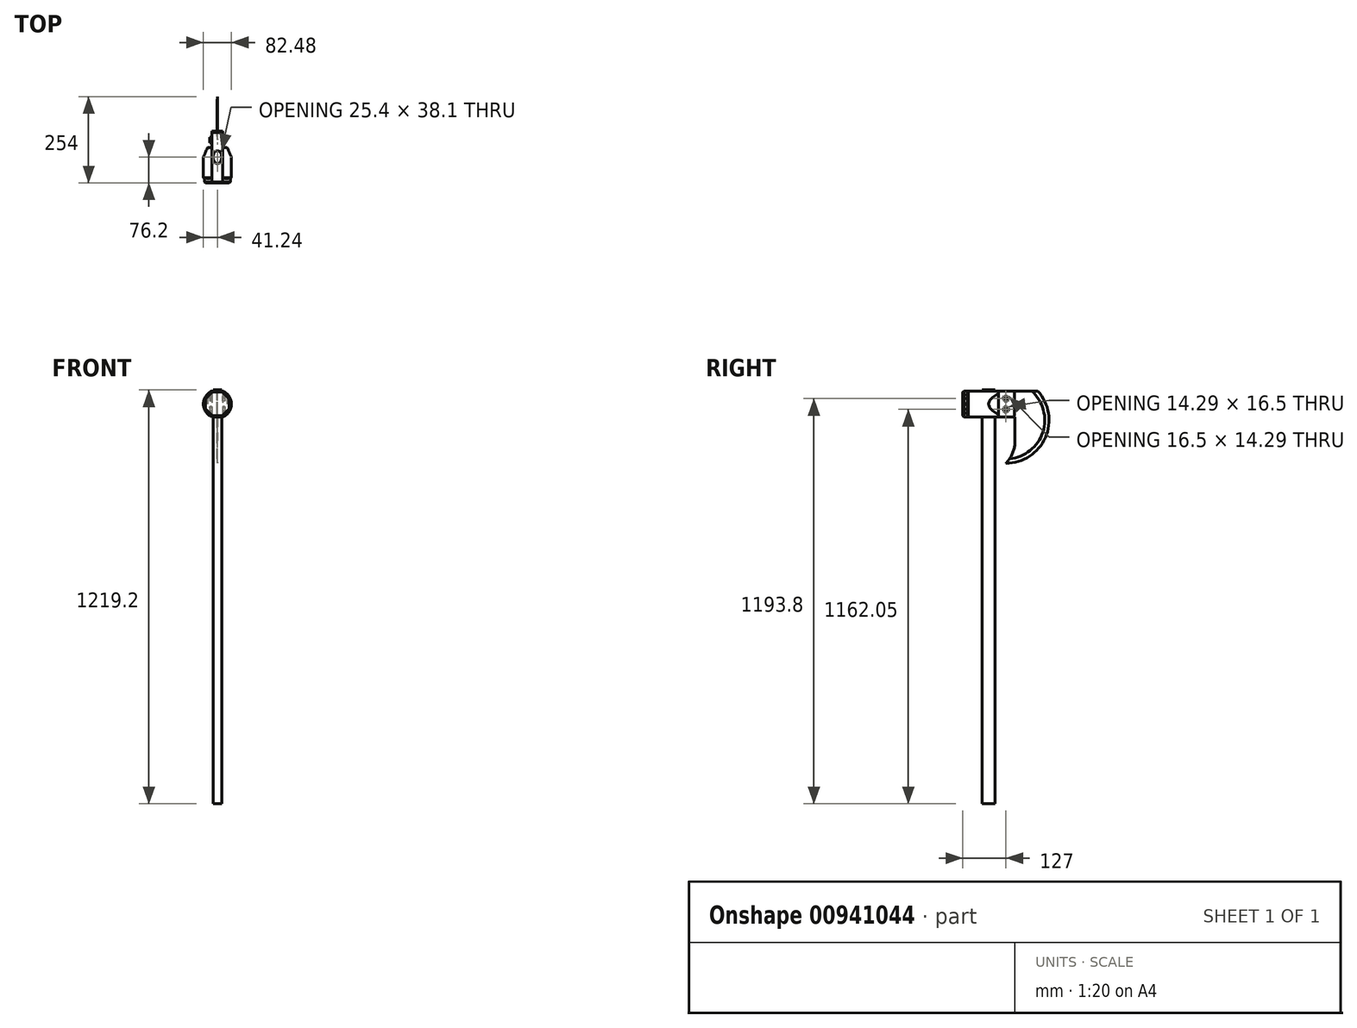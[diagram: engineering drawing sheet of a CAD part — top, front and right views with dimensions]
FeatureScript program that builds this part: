
annotation { "Feature Type Name" : "Feature", "Feature Type Description" : "" }
export const myFeature = defineFeature(function(context is Context, id is Id, definition is map)
    precondition{}
    {
        {
            var Q0;
            Q0=qCreatedBy(makeId("Top.planeOp"),FACE);
            var sketch = newSketch(context, id + "F0", { "sketchPlane" : qUnion([Q0])});
            skEllipse(sketch, "E0", {"center": v(0, 0) * mm, "majorRadius": 12.7 * mm, "minorRadius": 19.05 * mm, "majorAxis": v(1, 0)});
            skSolve(sketch);
        }
        {
            var Q0;
            Q0 = qSketchRegion(id + "F0", true);
            extrude(context, id + "F1", {"entities" : qUnion([Q0]), "depth" : 1219.2 * mm, "offsetDistance" : 25.4 * mm});
        }
        {
            var Q0;
            Q0=qCreatedBy(makeId("Front.planeOp"),FACE);
            var sketch = newSketch(context, id + "F2", { "sketchPlane" : qUnion([Q0])});
            skCircle(sketch, "E1.cCircle", {"center": v(0, 1177.93) * mm, "radius": 41.24 * mm});
            skLineSegment(sketch, "E1.0", {"start": v(15.78, 1139.83) * mm, "end": v(-15.78, 1139.83) * mm});
            skLineSegment(sketch, "E1.1", {"start": v(-15.78, 1139.83) * mm, "end": v(-38.1, 1162.14) * mm});
            skLineSegment(sketch, "E1.2", {"start": v(-38.1, 1162.14) * mm, "end": v(-38.1, 1193.7) * mm});
            skLineSegment(sketch, "E1.3", {"start": v(-38.1, 1193.7) * mm, "end": v(-15.78, 1216.03) * mm});
            skLineSegment(sketch, "E1.4", {"start": v(-15.78, 1216.03) * mm, "end": v(15.78, 1216.03) * mm});
            skLineSegment(sketch, "E1.5", {"start": v(15.78, 1216.03) * mm, "end": v(38.1, 1193.7) * mm});
            skLineSegment(sketch, "E1.6", {"start": v(38.1, 1193.7) * mm, "end": v(38.1, 1162.14) * mm});
            skLineSegment(sketch, "E1.7", {"start": v(38.1, 1162.14) * mm, "end": v(15.78, 1139.83) * mm});
            skSolve(sketch);
        }
        {
            var Q0;
            Q0=makeQuery(id+"F2.imprint","IMPRINT",FACE,{"disambiguationData":[TD([[makeQuery(id+"F2.imprint","IMPRINT",EDGE,{"derivedFrom":sQuery(id+"F2.wireOp",EDGE,"E1.0")}),-1.0]])]});
            extrude(context, id + "F3", {"entities" : qUnion([Q0]), "operationType" : NewBodyOperationType.ADD, "depth" : 76.2 * mm, "offsetDistance" : 25.4 * mm, "hasSecondDirection" : true, "secondDirectionOppositeDirection" : true, "secondDirectionDepth" : 76.2 * mm});
        }
        {
            var Q0;
            {var subQ0=sQuery(id+"F2.wireOp",EDGE,"E1.5");Q0=makeQuery(id+"F2.imprint","IMPRINT",FACE,{"disambiguationData":[TD([[makeQuery(id+"F2.imprint","IMPRINT",EDGE,{"derivedFrom":subQ0}),1.0]])]});}
            var Q1;
            {var subQ0=sQuery(id+"F2.wireOp",EDGE,"E1.6");Q1=makeQuery(id+"F2.imprint","IMPRINT",FACE,{"disambiguationData":[TD([[makeQuery(id+"F2.imprint","IMPRINT",EDGE,{"derivedFrom":subQ0}),1.0]])]});}
            var Q2;
            {var subQ0=sQuery(id+"F2.wireOp",EDGE,"E1.7");Q2=makeQuery(id+"F2.imprint","IMPRINT",FACE,{"disambiguationData":[TD([[makeQuery(id+"F2.imprint","IMPRINT",EDGE,{"derivedFrom":subQ0}),1.0]])]});}
            var Q3;
            {var subQ0=sQuery(id+"F2.wireOp",EDGE,"E1.1");Q3=makeQuery(id+"F2.imprint","IMPRINT",FACE,{"disambiguationData":[TD([[makeQuery(id+"F2.imprint","IMPRINT",EDGE,{"derivedFrom":subQ0}),1.0]])]});}
            var Q4;
            {var subQ0=sQuery(id+"F2.wireOp",EDGE,"E1.2");Q4=makeQuery(id+"F2.imprint","IMPRINT",FACE,{"disambiguationData":[TD([[makeQuery(id+"F2.imprint","IMPRINT",EDGE,{"derivedFrom":subQ0}),1.0]])]});}
            var Q5;
            {var subQ0=sQuery(id+"F2.wireOp",EDGE,"E1.3");Q5=makeQuery(id+"F2.imprint","IMPRINT",FACE,{"disambiguationData":[TD([[makeQuery(id+"F2.imprint","IMPRINT",EDGE,{"derivedFrom":subQ0}),1.0]])]});}
            extrude(context, id + "F4", {"entities" : qUnion([Q0, Q1, Q2, Q3, Q4, Q5]), "operationType" : NewBodyOperationType.ADD, "depth" : 63.5 * mm, "offsetDistance" : 25.4 * mm, "hasSecondDirection" : true, "secondDirectionOppositeDirection" : true, "secondDirectionDepth" : 63.5 * mm});
        }
        {
            var Q0;
            Q0=makeQuery(id+"F3.opExtrude","CAP_FACE",FACE,{"disambiguationData":[OSD([sQuery(id+"F2.wireOp",EDGE,"E1.0"),sQuery(id+"F2.wireOp",EDGE,"E1.1"),sQuery(id+"F2.wireOp",EDGE,"E1.2"),sQuery(id+"F2.wireOp",EDGE,"E1.3"),sQuery(id+"F2.wireOp",EDGE,"E1.4"),sQuery(id+"F2.wireOp",EDGE,"E1.5"),sQuery(id+"F2.wireOp",EDGE,"E1.6"),sQuery(id+"F2.wireOp",EDGE,"E1.7")])],"isStart":false});
            var Q1;
            Q1=makeQuery(id+"F3.opExtrude","CAP_FACE",FACE,{"disambiguationData":[OSD([sQuery(id+"F2.wireOp",EDGE,"E1.0"),sQuery(id+"F2.wireOp",EDGE,"E1.1"),sQuery(id+"F2.wireOp",EDGE,"E1.2"),sQuery(id+"F2.wireOp",EDGE,"E1.3"),sQuery(id+"F2.wireOp",EDGE,"E1.4"),sQuery(id+"F2.wireOp",EDGE,"E1.5"),sQuery(id+"F2.wireOp",EDGE,"E1.6"),sQuery(id+"F2.wireOp",EDGE,"E1.7")])],"isStart":true});
            chamfer(context, id + "F5", {"entities" : qUnion([Q0, Q1]), "width" : 3.17 * mm, "tangentPropagation" : true});
        }
        {
            var Q0;
            {var subQ0=sQuery(id+"F2.wireOp",EDGE,"E1.3");var subQ1=sQuery(id+"F2.wireOp",EDGE,"E1.cCircle");Q0=makeQuery(id+"F4.opExtrude","CAP_EDGE",EDGE,{"disambiguationData":[OSD([subQ1]),TDD([makeQuery(id+"F2.imprint","IMPRINT",EDGE,{"disambiguationData":[TD([[makeQuery(id+"F2.imprint","INTERSECT",VERTEX,{"derivedFrom":[subQ1,sQuery(id+"F2.wireOp",EDGE,"E1.2"),subQ0]}),1.0]])],"derivedFrom":subQ1})])],"isStart":true});}
            var Q1;
            {var subQ0=sQuery(id+"F2.wireOp",EDGE,"E1.2");var subQ1=sQuery(id+"F2.wireOp",EDGE,"E1.cCircle");Q1=makeQuery(id+"F4.opExtrude","CAP_EDGE",EDGE,{"disambiguationData":[OSD([subQ1]),TDD([makeQuery(id+"F2.imprint","IMPRINT",EDGE,{"disambiguationData":[TD([[makeQuery(id+"F2.imprint","INTERSECT",VERTEX,{"derivedFrom":[subQ1,sQuery(id+"F2.wireOp",EDGE,"E1.1"),subQ0]}),1.0]])],"derivedFrom":subQ1})])],"isStart":true});}
            var Q2;
            {var subQ0=sQuery(id+"F2.wireOp",EDGE,"E1.1");var subQ1=sQuery(id+"F2.wireOp",EDGE,"E1.cCircle");Q2=makeQuery(id+"F4.opExtrude","CAP_EDGE",EDGE,{"disambiguationData":[OSD([subQ1]),TDD([makeQuery(id+"F2.imprint","IMPRINT",EDGE,{"disambiguationData":[TD([[makeQuery(id+"F2.imprint","INTERSECT",VERTEX,{"derivedFrom":[subQ1,sQuery(id+"F2.wireOp",EDGE,"E1.0"),subQ0]}),1.0]])],"derivedFrom":subQ1})])],"isStart":true});}
            var Q3;
            {var subQ0=sQuery(id+"F2.wireOp",EDGE,"E1.5");var subQ1=sQuery(id+"F2.wireOp",EDGE,"E1.cCircle");Q3=makeQuery(id+"F4.opExtrude","CAP_EDGE",EDGE,{"disambiguationData":[OSD([subQ1]),TDD([makeQuery(id+"F2.imprint","IMPRINT",EDGE,{"disambiguationData":[TD([[makeQuery(id+"F2.imprint","INTERSECT",VERTEX,{"derivedFrom":[subQ1,sQuery(id+"F2.wireOp",EDGE,"E1.4"),subQ0]}),1.0]])],"derivedFrom":subQ1})])],"isStart":true});}
            var Q4;
            {var subQ0=sQuery(id+"F2.wireOp",EDGE,"E1.6");var subQ1=sQuery(id+"F2.wireOp",EDGE,"E1.cCircle");Q4=makeQuery(id+"F4.opExtrude","CAP_EDGE",EDGE,{"disambiguationData":[OSD([subQ1]),TDD([makeQuery(id+"F2.imprint","IMPRINT",EDGE,{"disambiguationData":[TD([[makeQuery(id+"F2.imprint","INTERSECT",VERTEX,{"derivedFrom":[subQ1,sQuery(id+"F2.wireOp",EDGE,"E1.5"),subQ0]}),1.0]])],"derivedFrom":subQ1})])],"isStart":true});}
            var Q5;
            {var subQ0=sQuery(id+"F2.wireOp",EDGE,"E1.7");var subQ1=sQuery(id+"F2.wireOp",EDGE,"E1.cCircle");Q5=makeQuery(id+"F4.opExtrude","CAP_EDGE",EDGE,{"disambiguationData":[OSD([subQ1]),TDD([makeQuery(id+"F2.imprint","IMPRINT",EDGE,{"disambiguationData":[TD([[makeQuery(id+"F2.imprint","INTERSECT",VERTEX,{"derivedFrom":[subQ1,sQuery(id+"F2.wireOp",EDGE,"E1.0"),subQ0]}),-1.0]])],"derivedFrom":subQ1})])],"isStart":true});}
            var Q6;
            {var subQ0=sQuery(id+"F2.wireOp",EDGE,"E1.5");var subQ1=sQuery(id+"F2.wireOp",EDGE,"E1.cCircle");Q6=makeQuery(id+"F4.opExtrude","CAP_EDGE",EDGE,{"disambiguationData":[OSD([subQ1]),TDD([makeQuery(id+"F2.imprint","IMPRINT",EDGE,{"disambiguationData":[TD([[makeQuery(id+"F2.imprint","INTERSECT",VERTEX,{"derivedFrom":[subQ1,sQuery(id+"F2.wireOp",EDGE,"E1.4"),subQ0]}),1.0]])],"derivedFrom":subQ1})])],"isStart":false});}
            var Q7;
            {var subQ0=sQuery(id+"F2.wireOp",EDGE,"E1.6");var subQ1=sQuery(id+"F2.wireOp",EDGE,"E1.cCircle");Q7=makeQuery(id+"F4.opExtrude","CAP_EDGE",EDGE,{"disambiguationData":[OSD([subQ1]),TDD([makeQuery(id+"F2.imprint","IMPRINT",EDGE,{"disambiguationData":[TD([[makeQuery(id+"F2.imprint","INTERSECT",VERTEX,{"derivedFrom":[subQ1,sQuery(id+"F2.wireOp",EDGE,"E1.5"),subQ0]}),1.0]])],"derivedFrom":subQ1})])],"isStart":false});}
            var Q8;
            {var subQ0=sQuery(id+"F2.wireOp",EDGE,"E1.7");var subQ1=sQuery(id+"F2.wireOp",EDGE,"E1.cCircle");Q8=makeQuery(id+"F4.opExtrude","CAP_EDGE",EDGE,{"disambiguationData":[OSD([subQ1]),TDD([makeQuery(id+"F2.imprint","IMPRINT",EDGE,{"disambiguationData":[TD([[makeQuery(id+"F2.imprint","INTERSECT",VERTEX,{"derivedFrom":[subQ1,sQuery(id+"F2.wireOp",EDGE,"E1.0"),subQ0]}),-1.0]])],"derivedFrom":subQ1})])],"isStart":false});}
            var Q9;
            {var subQ0=sQuery(id+"F2.wireOp",EDGE,"E1.3");var subQ1=sQuery(id+"F2.wireOp",EDGE,"E1.cCircle");Q9=makeQuery(id+"F4.opExtrude","CAP_EDGE",EDGE,{"disambiguationData":[OSD([subQ1]),TDD([makeQuery(id+"F2.imprint","IMPRINT",EDGE,{"disambiguationData":[TD([[makeQuery(id+"F2.imprint","INTERSECT",VERTEX,{"derivedFrom":[subQ1,sQuery(id+"F2.wireOp",EDGE,"E1.2"),subQ0]}),1.0]])],"derivedFrom":subQ1})])],"isStart":false});}
            var Q10;
            {var subQ0=sQuery(id+"F2.wireOp",EDGE,"E1.2");var subQ1=sQuery(id+"F2.wireOp",EDGE,"E1.cCircle");Q10=makeQuery(id+"F4.opExtrude","CAP_EDGE",EDGE,{"disambiguationData":[OSD([subQ1]),TDD([makeQuery(id+"F2.imprint","IMPRINT",EDGE,{"disambiguationData":[TD([[makeQuery(id+"F2.imprint","INTERSECT",VERTEX,{"derivedFrom":[subQ1,sQuery(id+"F2.wireOp",EDGE,"E1.1"),subQ0]}),1.0]])],"derivedFrom":subQ1})])],"isStart":false});}
            var Q11;
            {var subQ0=sQuery(id+"F2.wireOp",EDGE,"E1.1");var subQ1=sQuery(id+"F2.wireOp",EDGE,"E1.cCircle");Q11=makeQuery(id+"F4.opExtrude","CAP_EDGE",EDGE,{"disambiguationData":[OSD([subQ1]),TDD([makeQuery(id+"F2.imprint","IMPRINT",EDGE,{"disambiguationData":[TD([[makeQuery(id+"F2.imprint","INTERSECT",VERTEX,{"derivedFrom":[subQ1,sQuery(id+"F2.wireOp",EDGE,"E1.0"),subQ0]}),1.0]])],"derivedFrom":subQ1})])],"isStart":false});}
            chamfer(context, id + "F6", {"entities" : qUnion([Q0, Q1, Q2, Q3, Q4, Q5, Q6, Q7, Q8, Q9, Q10, Q11]), "width" : 3.12 * mm});
        }
        {
            var Q0;
            Q0=qCreatedBy(makeId("Right.planeOp"),FACE);
            var sketch = newSketch(context, id + "F7", { "sketchPlane" : qUnion([Q0])});
            skCircle(sketch, "E2", {"center": v(50.8, 1130.3) * mm, "radius": 127 * mm});
            skPoint(sketch, "E3.start.orphan", {"position": v(50.8, 1003.3) * mm});
            skLineSegment(sketch, "E4", {"start": v(30.16, 1216.03) * mm, "end": v(30.16, 1139.83) * mm});
            skLineSegment(sketch, "E5", {"start": v(30.16, 1216.03) * mm, "end": v(144.5, 1216.03) * mm});
            skLineSegment(sketch, "E6", {"start": v(30.16, 1139.83) * mm, "end": v(77.79, 1139.83) * mm});
            skLineSegment(sketch, "E7", {"start": v(77.79, 1139.83) * mm, "end": v(77.79, 1069.98) * mm});
            skArc(sketch, "E8", {"start": v(50.8, 1003.3) * mm, "mid": v(70.78, 1034.01) * mm, "end": v(77.79, 1069.98) * mm});
            skSolve(sketch);
        }
        {
            var Q0;
            Q0=makeQuery(id+"F7.imprint","IMPRINT",FACE,{"disambiguationData":[TD([[makeQuery(id+"F7.imprint","IMPRINT",EDGE,{"derivedFrom":sQuery(id+"F7.wireOp",EDGE,"E4")}),1.0]])]});
            extrude(context, id + "F8", {"entities" : qUnion([Q0]), "operationType" : NewBodyOperationType.ADD, "depth" : 0.8 * mm, "offsetDistance" : 25.4 * mm, "hasSecondDirection" : true, "secondDirectionOppositeDirection" : true, "secondDirectionDepth" : 0.8 * mm});
        }
        {
            var Q0;
            Q0=qCreatedBy(makeId("Top.planeOp"),FACE);
            var sketch = newSketch(context, id + "F9", { "sketchPlane" : qUnion([Q0])});
            skLineSegment(sketch, "E9.bottom", {"start": v(28.58, 28.57) * mm, "end": v(15.88, 28.57) * mm});
            skLineSegment(sketch, "E9.top", {"start": v(41.28, 76.2) * mm, "end": v(15.88, 76.2) * mm});
            skLineSegment(sketch, "E9.left", {"start": v(41.27, 28.57) * mm, "end": v(41.28, 76.2) * mm});
            skLineSegment(sketch, "E9.right", {"start": v(-41.28, 28.57) * mm, "end": v(-41.28, 76.2) * mm});
            skPoint(sketch, "E9.middle", {"position": v(0, 52.39) * mm});
            skLineSegment(sketch, "E10.left", {"start": v(15.88, 28.58) * mm, "end": v(15.88, 76.2) * mm});
            skLineSegment(sketch, "E10.right", {"start": v(-15.88, 28.58) * mm, "end": v(-15.88, 76.2) * mm});
            skLineSegment(sketch, "E11.trimOffspring", {"start": v(-15.88, 76.2) * mm, "end": v(-41.28, 76.2) * mm});
            skLineSegment(sketch, "E12.trimOffspring", {"start": v(-15.87, 28.57) * mm, "end": v(-28.58, 28.57) * mm});
            skLineSegment(sketch, "E13", {"start": v(28.58, 28.57) * mm, "end": v(41.27, 0) * mm});
            skLineSegment(sketch, "E14", {"start": v(41.27, 0) * mm, "end": v(41.27, 28.57) * mm});
            skLineSegment(sketch, "E15", {"start": v(-28.58, 28.57) * mm, "end": v(-41.28, 0) * mm});
            skLineSegment(sketch, "E16", {"start": v(-41.28, 0) * mm, "end": v(-41.28, 28.57) * mm});
            skSolve(sketch);
        }
        {
            var Q0;
            Q0 = qSketchRegion(id + "F9", true);
            extrude(context, id + "F10", {"entities" : qUnion([Q0]), "operationType" : NewBodyOperationType.REMOVE, "depth" : 1219.2 * mm, "offsetDistance" : 25.4 * mm});
        }
        {
            var Q0;
            Q0=qCreatedBy(makeId("Right.planeOp"),FACE);
            var sketch = newSketch(context, id + "F11", { "sketchPlane" : qUnion([Q0])});
            skCircle(sketch, "E17.cCircle", {"center": v(50.8, 1193.8) * mm, "radius": 7.14 * mm, "construction": true});
            skLineSegment(sketch, "E17.0", {"start": v(59.05, 1193.8) * mm, "end": v(54.92, 1186.66) * mm});
            skLineSegment(sketch, "E17.1", {"start": v(54.92, 1186.66) * mm, "end": v(46.68, 1186.66) * mm});
            skLineSegment(sketch, "E17.2", {"start": v(46.68, 1186.66) * mm, "end": v(42.55, 1193.8) * mm});
            skLineSegment(sketch, "E17.3", {"start": v(42.55, 1193.8) * mm, "end": v(46.68, 1200.94) * mm});
            skLineSegment(sketch, "E17.4", {"start": v(46.68, 1200.94) * mm, "end": v(54.92, 1200.94) * mm});
            skLineSegment(sketch, "E17.5", {"start": v(54.92, 1200.94) * mm, "end": v(59.05, 1193.8) * mm});
            skPoint(sketch, "E17.0.midPoint", {"position": v(56.99, 1190.23) * mm});
            skCircle(sketch, "E18.cCircle", {"center": v(50.8, 1162.05) * mm, "radius": 7.14 * mm, "construction": true});
            skLineSegment(sketch, "E18.0", {"start": v(57.94, 1166.17) * mm, "end": v(57.94, 1157.93) * mm});
            skLineSegment(sketch, "E18.1", {"start": v(57.94, 1157.93) * mm, "end": v(50.8, 1153.8) * mm});
            skLineSegment(sketch, "E18.2", {"start": v(50.8, 1153.8) * mm, "end": v(43.66, 1157.93) * mm});
            skLineSegment(sketch, "E18.3", {"start": v(43.66, 1157.93) * mm, "end": v(43.66, 1166.17) * mm});
            skLineSegment(sketch, "E18.4", {"start": v(43.66, 1166.17) * mm, "end": v(50.8, 1170.3) * mm});
            skLineSegment(sketch, "E18.5", {"start": v(50.8, 1170.3) * mm, "end": v(57.94, 1166.17) * mm});
            skPoint(sketch, "E18.0.midPoint", {"position": v(57.94, 1162.05) * mm});
            skSolve(sketch);
        }
        {
            var Q0;
            Q0 = qSketchRegion(id + "F11", true);
            extrude(context, id + "F12", {"entities" : qUnion([Q0]), "operationType" : NewBodyOperationType.ADD, "depth" : 22.22 * mm, "offsetDistance" : 25.4 * mm, "hasSecondDirection" : true, "secondDirectionOppositeDirection" : true, "secondDirectionDepth" : 22.22 * mm});
        }
        {
            var Q0;
            Q0=makeQuery(id+"F8.opExtrude","CAP_EDGE",EDGE,{"disambiguationData":[OSD([sQuery(id+"F7.wireOp",EDGE,"E2")])],"isStart":true});
            chamfer(context, id + "F13", {"entities" : qUnion([Q0]), "chamferType" : ChamferType.TWO_OFFSETS, "width1" : 0.8 * mm, "oppositeDirection" : false, "width2" : 12.7 * mm, "tangentPropagation" : true});
        }
        {
            var Q0;
            Q0=makeQuery(id+"F8.opExtrude","CAP_EDGE",EDGE,{"disambiguationData":[OSD([sQuery(id+"F7.wireOp",EDGE,"E2")])],"isStart":false});
            chamfer(context, id + "F14", {"entities" : qUnion([Q0]), "chamferType" : ChamferType.TWO_OFFSETS, "width1" : 12.7 * mm, "oppositeDirection" : false, "width2" : 0.8 * mm, "tangentPropagation" : true});
        }
    });
